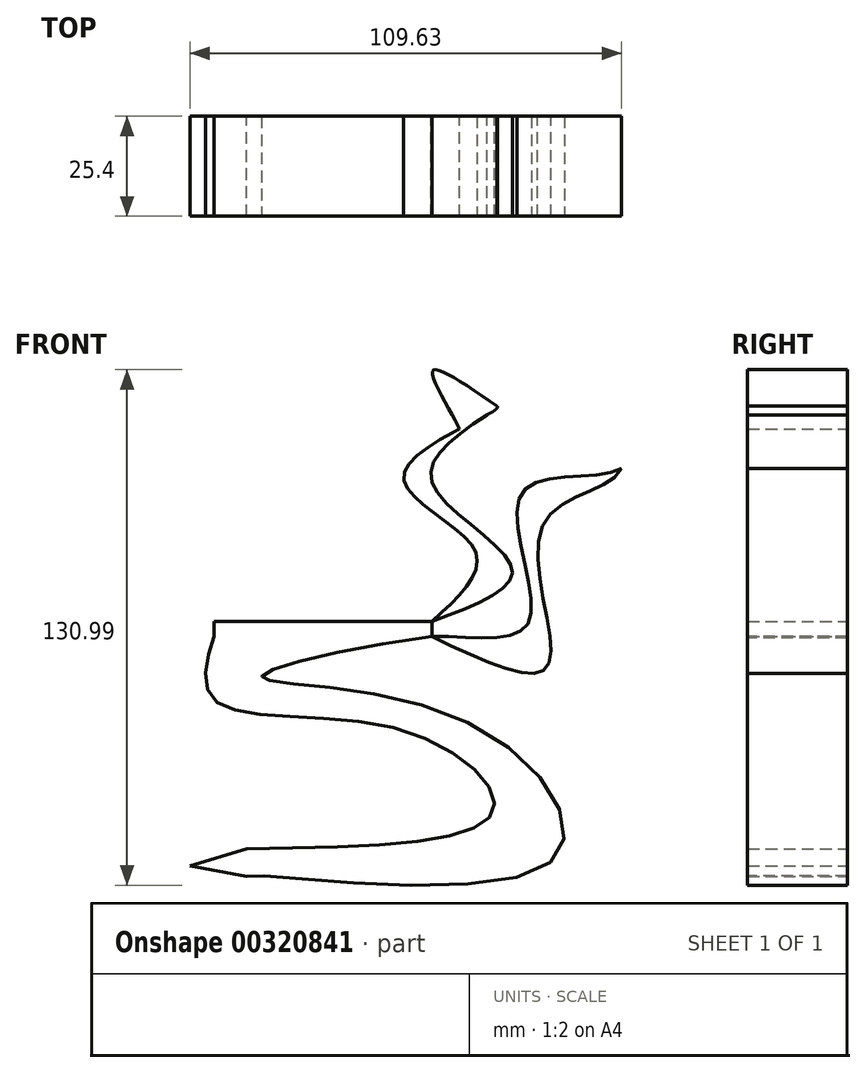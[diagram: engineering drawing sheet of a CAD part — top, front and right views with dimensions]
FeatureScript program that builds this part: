
annotation { "Feature Type Name" : "Feature", "Feature Type Description" : "" }
export const myFeature = defineFeature(function(context is Context, id is Id, definition is map)
    precondition{}
    {
        {
            var Q0;
            Q0=qCreatedBy(makeId("Front.planeOp"),FACE);
            var sketch = newSketch(context, id + "F0", { "sketchPlane" : qUnion([Q0])});
            skLineSegment(sketch, "E0.bottom", {"start": v(0, 0) * mm, "end": v(-55.43, 0) * mm});
            skLineSegment(sketch, "E0.top", {"start": v(0, -3.88) * mm, "end": v(-55.43, -3.88) * mm});
            skLineSegment(sketch, "E0.left", {"start": v(0, 0) * mm, "end": v(0, -3.88) * mm});
            skLineSegment(sketch, "E0.right", {"start": v(-55.43, 0) * mm, "end": v(-55.43, -3.88) * mm});
            skFitSpline(sketch, "E1", {"points": [v(-55.43, -3.88) * mm, v(-55.43, -19.98) * mm, v(-7.14, -27.81) * mm, v(15.48, -48.26) * mm, v(-47.17, -57.83) * mm], "startDerivative": vector(-31.4, -100.31) * mm, "endDerivative": vector(-269.18, -4.07) * mm});
            skFitSpline(sketch, "E2", {"points": [v(0, -3.88) * mm, v(-43.25, -14.32) * mm, v(9.83, -26.07) * mm, v(29.4, -61.74) * mm, v(-47.17, -64.79) * mm, v(-47.17, -65.23) * mm], "startDerivative": vector(-299.77, -38.7) * mm, "endDerivative": vector(14.3, -22.33) * mm});
            skFitSpline(sketch, "E3", {"points": [v(-47.17, -57.83) * mm, v(-47.17, -64.79) * mm], "startDerivative": vector(0, -6.96) * mm, "endDerivative": vector(0, -6.96) * mm});
            skLineSegment(sketch, "E4", {"start": v(-47.17, -57.83) * mm, "end": v(-61.52, -62.18) * mm});
            skLineSegment(sketch, "E5", {"start": v(-61.52, -62.18) * mm, "end": v(-47.17, -64.79) * mm});
            skLineSegment(sketch, "E6", {"start": v(-55.43, 0) * mm, "end": v(-32.8, 0) * mm});
            skFitSpline(sketch, "E7", {"points": [v(0, 0) * mm, v(10.7, 18.3) * mm, v(-7.14, 37.45) * mm, v(16.35, 53.98) * mm, v(16.35, 54.85) * mm], "startDerivative": vector(71.85, 64.9) * mm, "endDerivative": vector(-9.34, 12.26) * mm});
            skFitSpline(sketch, "E8", {"points": [v(0, 0) * mm, v(20.27, 13.52) * mm, v(0, 35.27) * mm, v(16.35, 53.98) * mm], "startDerivative": vector(100.96, 36.96) * mm, "endDerivative": vector(86.1, 55.47) * mm});
            skFitSpline(sketch, "E9", {"points": [v(0, -3.88) * mm, v(24.62, 0) * mm, v(22.88, 32.66) * mm, v(48.1, 38.75) * mm], "startDerivative": vector(94.31, 2.37) * mm, "endDerivative": vector(52.96, 31.01) * mm});
            skFitSpline(sketch, "E10", {"points": [v(0, -3.88) * mm, v(29.4, -11.28) * mm, v(28.1, 24.4) * mm, v(48.1, 38.75) * mm], "startDerivative": vector(110.27, -53.73) * mm, "endDerivative": vector(28.92, 57.54) * mm});
            skFitSpline(sketch, "E11", {"points": [v(16.53, 54.61) * mm, v(0, 63.11) * mm, v(7.05, 47.98) * mm, v(5.33, 47.98) * mm], "startDerivative": vector(-55.62, 38.57) * mm, "endDerivative": vector(-18.38, 6.6) * mm});
            skFitSpline(sketch, "E12", {"points": [v(48.1, 38.75) * mm, v(61.16, 32.96) * mm, v(45.2, 32.96) * mm], "startDerivative": vector(40.92, -14.8) * mm, "endDerivative": vector(-45.94, 3.06) * mm});
            skSolve(sketch);
        }
        {
            var Q0;
            Q0 = qSketchRegion(id + "F0", true);
            extrude(context, id + "F1", {"entities" : qUnion([Q0]), "depth" : 25.4 * mm});
        }
    });
